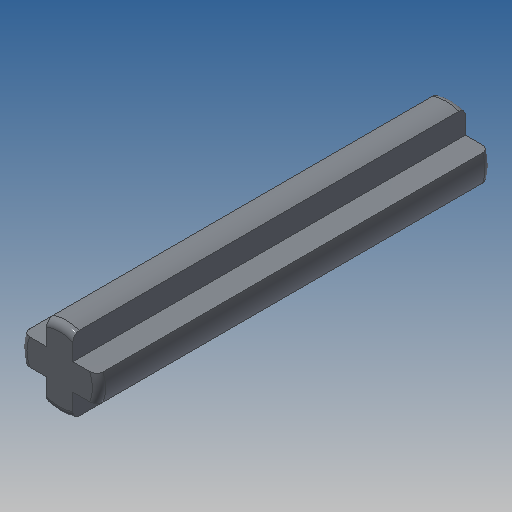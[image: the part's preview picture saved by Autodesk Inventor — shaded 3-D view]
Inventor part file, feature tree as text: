
AUTODESK INVENTOR PART (.ipt)
format: ipt  version: 2022.2 (Build 262287000, 287)  size: 145,408 bytes
history: native  units: in
note: dims shown in document units (in); Inventor stores cm internally (conversion verified against a paired STEP export)
features: extrude x1, fillet x1, sketch x1
ambient origin geometry x8: Origin, YZ Plane, XZ Plane, XY Plane, X Axis, Y Axis, Z Axis, Center Point
bodies: Solid1 (feature_tree)
feature tree (3):
  extrude  "Extrusion1"  Depth=0.0157in
  fillet  "Fillet1"  Radius=0.9449in
  sketch  "Sketch1"  dims[d0=0.189in d1=0.063in d2=0.9449in d3=0.0in d4=0.0157in d5=0.0in d6=0.0in]
